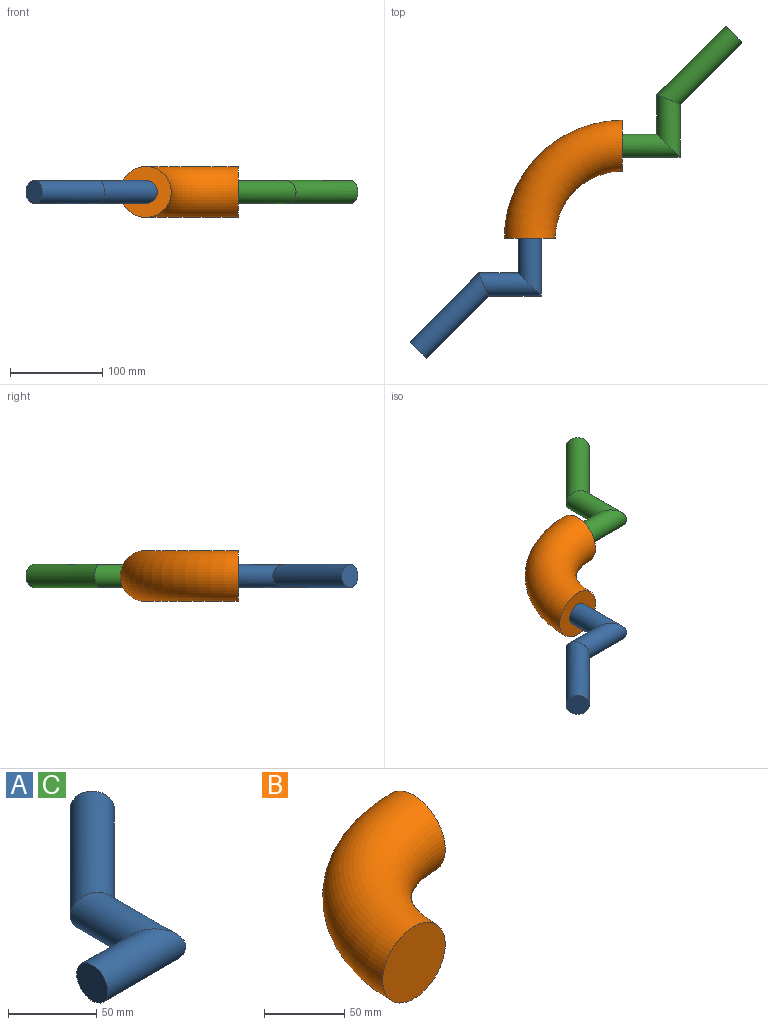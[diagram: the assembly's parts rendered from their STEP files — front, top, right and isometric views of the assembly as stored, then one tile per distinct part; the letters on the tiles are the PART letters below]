
ASSEMBLY  parts=3 mates=2
PART A: 5 faces, bbox 129.5x142x25 mm
  f0: plane 25x17.68mm, normal (0.71,0.71,0), area 490.9mm2, adj f2
  f1: plane 25x25mm, normal (-1,0,0), area 490.9mm2, adj f4
  f2: cylinder r=12.5mm len=92.05mm, axis (0.71,0.71,0), area 7854mm2, adj f0,f3
  f3: cylinder r=12.5mm len=67.68mm, axis (0,1,0), area 3927mm2, adj f2,f4
  f4: cylinder r=12.5mm len=62.5mm, axis (1,0,0), area 3927mm2, adj f1,f3
PART B: 3 faces, bbox 138x138x55 mm
  f0: plane 55x55mm, normal (0,-1,0), area 2375.8mm2, adj f2
  f1: plane 55x55mm, normal (1,0,0), area 2375.8mm2, adj f2
  f2: torus R=100mm, axis (0,0,-1), area 27141.4mm2, adj f0,f1
PART C: same geometry as A
PLACE A rot(axis=(0.71,-0.71,0),180deg) t=(-100,-100,0)mm
PLACE B t=(0,-100,0)mm
PLACE C at identity
MATE fastened A.f4 <-> B.f0  axis (0,1,0) through (-100,-100,0)mm
MATE fastened C.f4 <-> B.f1  axis (-1,0,0) through (0,0,0)mm
